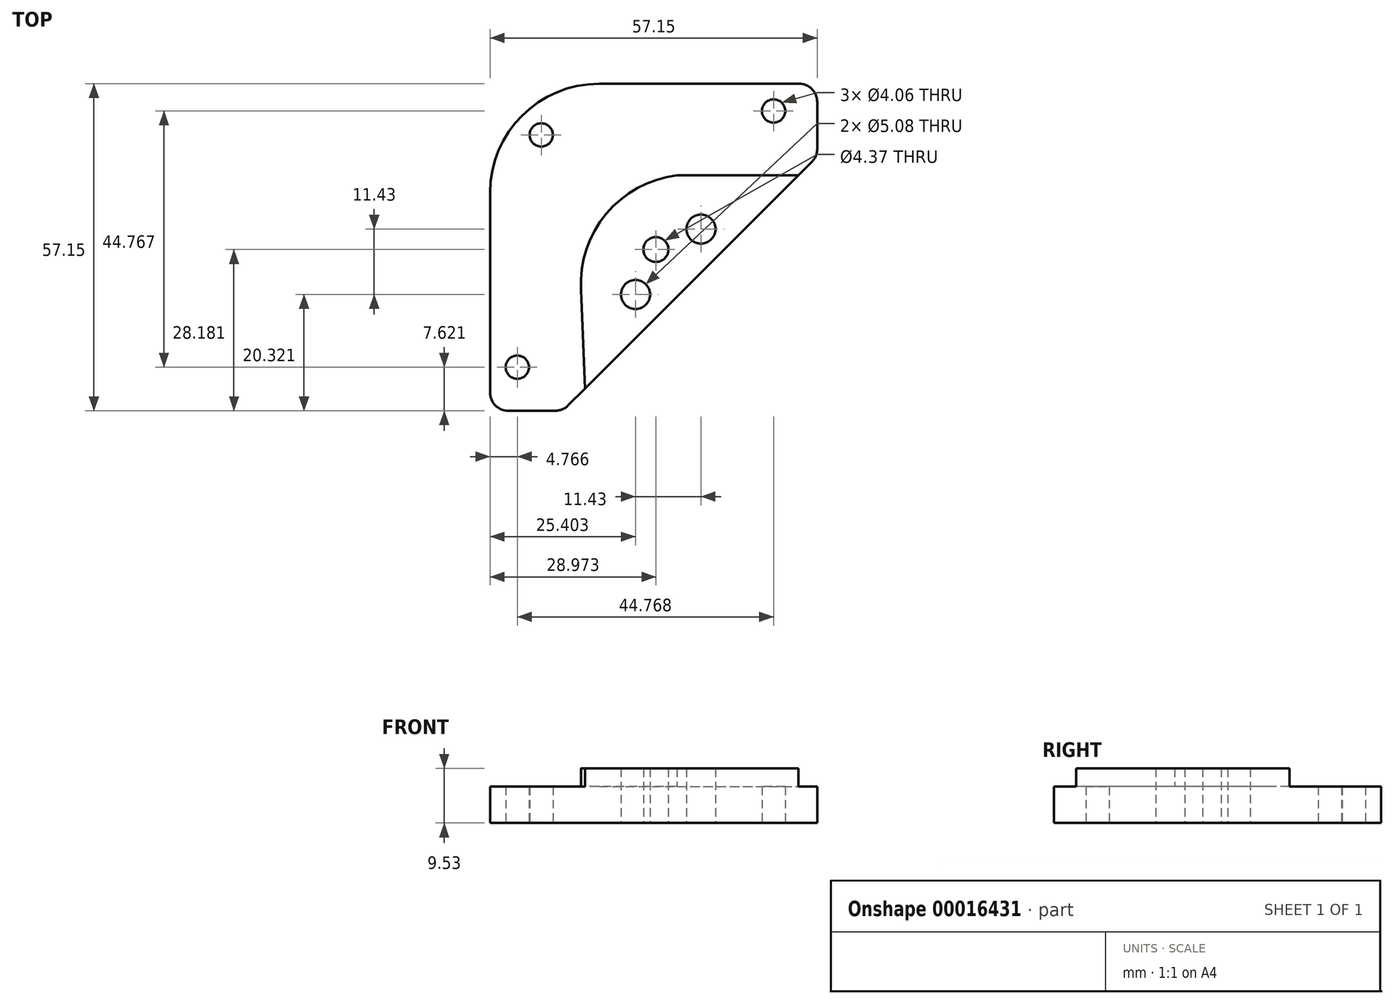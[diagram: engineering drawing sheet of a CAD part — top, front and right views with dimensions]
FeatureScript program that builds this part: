
annotation { "Feature Type Name" : "Feature", "Feature Type Description" : "" }
export const myFeature = defineFeature(function(context is Context, id is Id, definition is map)
    precondition{}
    {
        {
            var Q0;
            Q0=qCreatedBy(makeId("Top.planeOp"),FACE);
            var sketch = newSketch(context, id + "F0", { "sketchPlane" : qUnion([Q0])});
            skLineSegment(sketch, "E0.bottom", {"start": v(2.45, 41.84) * mm, "end": v(37.38, 41.84) * mm});
            skLineSegment(sketch, "E0.top", {"start": v(-13.42, -15.3) * mm, "end": v(-5.21, -15.3) * mm});
            skLineSegment(sketch, "E0.left", {"start": v(-16.6, 22.8) * mm, "end": v(-16.6, -12.13) * mm});
            skLineSegment(sketch, "E0.right", {"start": v(40.55, 38.67) * mm, "end": v(40.55, 30.46) * mm});
            skPoint(sketch, "E1.visualSharp", {"position": v(-16.6, 41.84) * mm});
            skArc(sketch, "E1.filletArc", {"start": v(2.45, 41.84) * mm, "mid": v(-11.02, 36.26) * mm, "end": v(-16.6, 22.8) * mm});
            skLineSegment(sketch, "E2", {"start": v(-2.97, -14.38) * mm, "end": v(39.62, 28.21) * mm});
            skCircle(sketch, "E3", {"center": v(8.8, 5.01) * mm, "radius": 2.54 * mm});
            skCircle(sketch, "E4", {"center": v(20.23, 16.44) * mm, "radius": 2.54 * mm});
            skPoint(sketch, "E5.visualSharp", {"position": v(-16.6, -15.3) * mm});
            skArc(sketch, "E5.filletArc", {"start": v(-16.6, -12.13) * mm, "mid": v(-15.67, -14.38) * mm, "end": v(-13.42, -15.3) * mm});
            skPoint(sketch, "E6.visualSharp", {"position": v(-3.9, -15.3) * mm});
            skArc(sketch, "E6.filletArc", {"start": v(-5.21, -15.3) * mm, "mid": v(-4, -15.07) * mm, "end": v(-2.97, -14.38) * mm});
            skPoint(sketch, "E7.visualSharp", {"position": v(40.55, 29.14) * mm});
            skArc(sketch, "E7.filletArc", {"start": v(39.62, 28.21) * mm, "mid": v(40.31, 29.24) * mm, "end": v(40.55, 30.46) * mm});
            skPoint(sketch, "E8.visualSharp", {"position": v(40.55, 41.84) * mm});
            skArc(sketch, "E8.filletArc", {"start": v(40.55, 38.67) * mm, "mid": v(39.62, 40.91) * mm, "end": v(37.38, 41.84) * mm});
            skLineSegment(sketch, "E9", {"start": v(-16.6, 41.84) * mm, "end": v(18.33, 6.92) * mm, "construction": true});
            skCircle(sketch, "E10", {"center": v(12.37, 12.87) * mm, "radius": 2.18 * mm});
            skCircle(sketch, "E11", {"center": v(-11.83, -7.69) * mm, "radius": 2.03 * mm});
            skCircle(sketch, "E12", {"center": v(32.93, 37.08) * mm, "radius": 2.03 * mm});
            skCircle(sketch, "E13", {"center": v(-7.65, 32.9) * mm, "radius": 2.03 * mm});
            skSolve(sketch);
        }
        {
            var Q0;
            Q0 = qSketchRegion(id + "F0", true);
            extrude(context, id + "F1", {"entities" : qUnion([Q0]), "depth" : 6.35 * mm});
        }
        {
            var Q0;
            Q0=makeQuery(id+"F1.opExtrude","CAP_FACE",FACE,{"disambiguationData":[OSD([sQuery(id+"F0.wireOp",EDGE,"E0.bottom"),sQuery(id+"F0.wireOp",EDGE,"E0.top"),sQuery(id+"F0.wireOp",EDGE,"E0.left"),sQuery(id+"F0.wireOp",EDGE,"E0.right"),sQuery(id+"F0.wireOp",EDGE,"E1.filletArc"),sQuery(id+"F0.wireOp",EDGE,"E2"),sQuery(id+"F0.wireOp",EDGE,"E3"),sQuery(id+"F0.wireOp",EDGE,"E4"),sQuery(id+"F0.wireOp",EDGE,"E5.filletArc"),sQuery(id+"F0.wireOp",EDGE,"E6.filletArc"),sQuery(id+"F0.wireOp",EDGE,"E7.filletArc"),sQuery(id+"F0.wireOp",EDGE,"E8.filletArc"),sQuery(id+"F0.wireOp",EDGE,"E10"),sQuery(id+"F0.wireOp",EDGE,"E11"),sQuery(id+"F0.wireOp",EDGE,"E12"),sQuery(id+"F0.wireOp",EDGE,"E13")])],"isStart":false});
            var sketch = newSketch(context, id + "F2", { "sketchPlane" : qUnion([Q0])});
            skLineSegment(sketch, "E14", {"start": v(-11.02, 36.26) * mm, "end": v(18.33, 6.92) * mm, "construction": true});
            skArc(sketch, "E15", {"start": v(16.05, 25.83) * mm, "mid": v(3.7, 19.11) * mm, "end": v(-0.69, 5.75) * mm});
            skLineSegment(sketch, "E16", {"start": v(4.86, -6.55) * mm, "end": v(31.8, 20.39) * mm});
            skLineSegment(sketch, "E17", {"start": v(-0.69, 5.75) * mm, "end": v(0, -11.41) * mm});
            skLineSegment(sketch, "E18", {"start": v(16.05, 25.83) * mm, "end": v(37.24, 25.83) * mm});
            skSolve(sketch);
        }
        {
            var Q0;
            {var subQ3=sQuery(id+"F2.wireOp",EDGE,"791a3a56-588c-482e-95a6-f595996b1ce0");Q0=makeQuery(id+"F2.imprint","IMPRINT",FACE,{"disambiguationData":[TD([[makeQuery(id+"F2.imprint","IMPRINT",EDGE,{"derivedFrom":subQ3}),-1.0]])]});}
            var Q1;
            Q1=makeQuery(id+"F2.imprint","IMPRINT",FACE,{"disambiguationData":[TD([[makeQuery(id+"F2.imprint","IMPRINT",EDGE,{"derivedFrom":sQuery(id+"F2.wireOp",EDGE,"E15")}),1.0]])]});
            extrude(context, id + "F3", {"entities" : qUnion([Q0, Q1]), "operationType" : NewBodyOperationType.ADD, "depth" : 3.17 * mm});
        }
    });
